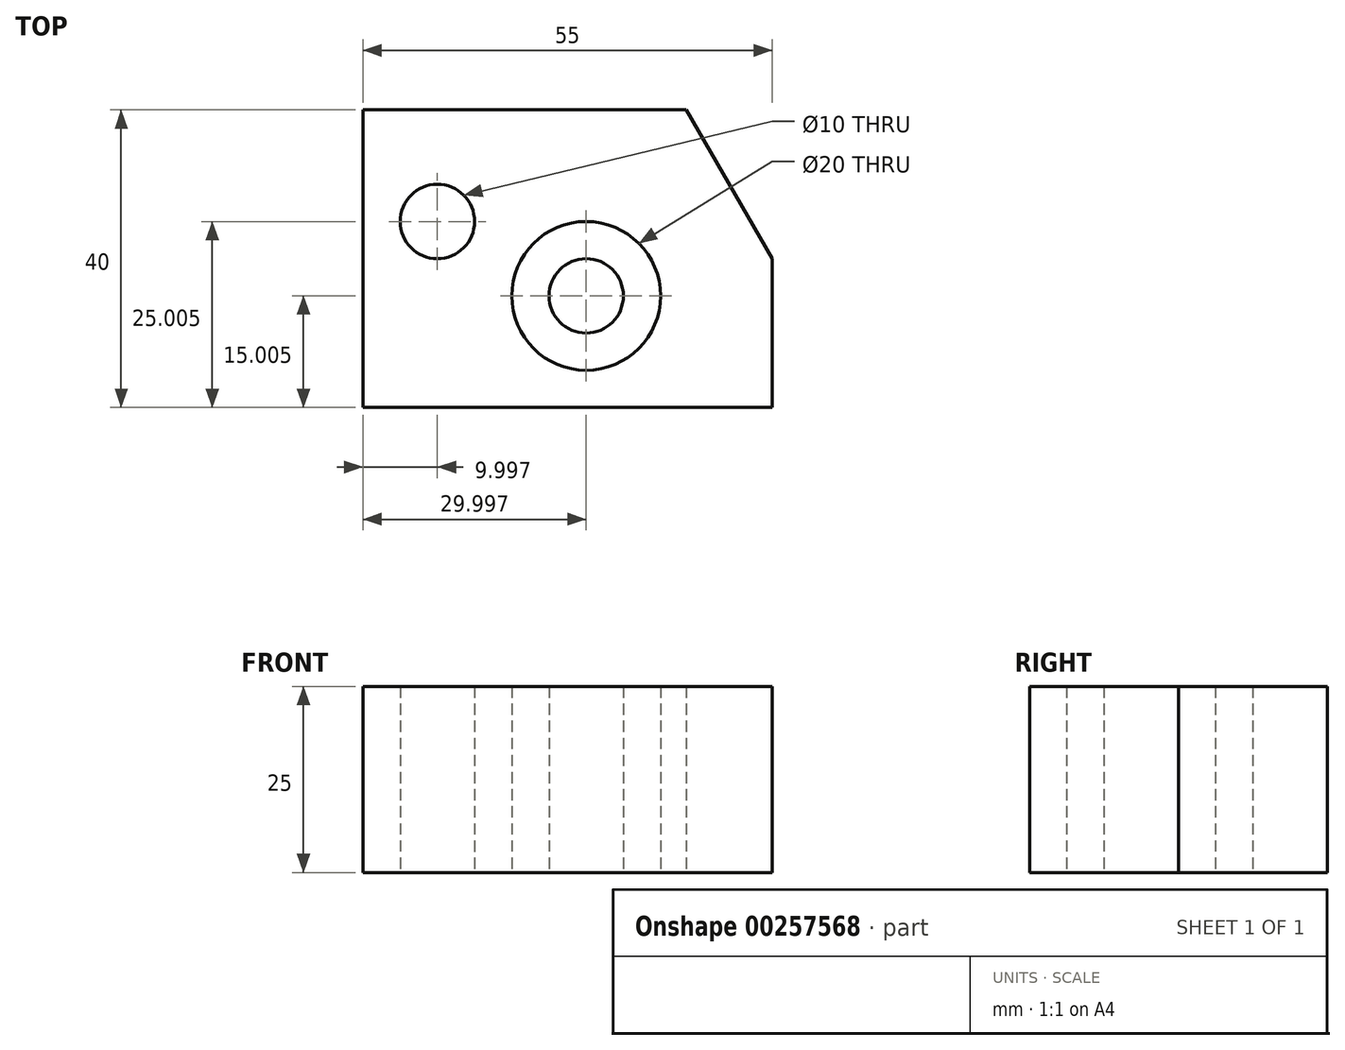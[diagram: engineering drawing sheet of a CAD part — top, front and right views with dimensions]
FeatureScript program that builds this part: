
annotation { "Feature Type Name" : "Feature", "Feature Type Description" : "" }
export const myFeature = defineFeature(function(context is Context, id is Id, definition is map)
    precondition{}
    {
        {
            var Q0;
            Q0=qCreatedBy(makeId("Top.planeOp"),FACE);
            var sketch = newSketch(context, id + "F0", { "sketchPlane" : qUnion([Q0])});
            skLineSegment(sketch, "E0", {"start": v(-27.51, 11.58) * mm, "end": v(-27.51, -28.42) * mm});
            skLineSegment(sketch, "E1", {"start": v(-27.51, -28.42) * mm, "end": v(27.49, -28.42) * mm});
            skLineSegment(sketch, "E2", {"start": v(27.49, -28.42) * mm, "end": v(27.49, -8.42) * mm});
            skLineSegment(sketch, "E3", {"start": v(27.49, -8.42) * mm, "end": v(15.94, 11.58) * mm});
            skLineSegment(sketch, "E4", {"start": v(15.94, 11.58) * mm, "end": v(-27.51, 11.58) * mm});
            skCircle(sketch, "E5", {"center": v(-17.51, -3.42) * mm, "radius": 5 * mm});
            skCircle(sketch, "E6", {"center": v(2.49, -13.42) * mm, "radius": 5 * mm});
            skCircle(sketch, "E7", {"center": v(2.49, -13.42) * mm, "radius": 10 * mm});
            skSolve(sketch);
        }
        {
            var Q0;
            Q0=makeQuery(id+"F0.imprint","IMPRINT",FACE,{"disambiguationData":[TD([[makeQuery(id+"F0.imprint","IMPRINT",EDGE,{"derivedFrom":sQuery(id+"F0.wireOp",EDGE,"E0")}),1.0]])]});
            var Q1;
            Q1=makeQuery(id+"F0.imprint","IMPRINT",FACE,{"disambiguationData":[TD([[makeQuery(id+"F0.imprint","IMPRINT",EDGE,{"derivedFrom":sQuery(id+"F0.wireOp",EDGE,"E6")}),1.0]])]});
            extrude(context, id + "F1", {"entities" : qUnion([Q0, Q1]), "depth" : 25 * mm});
        }
    });
